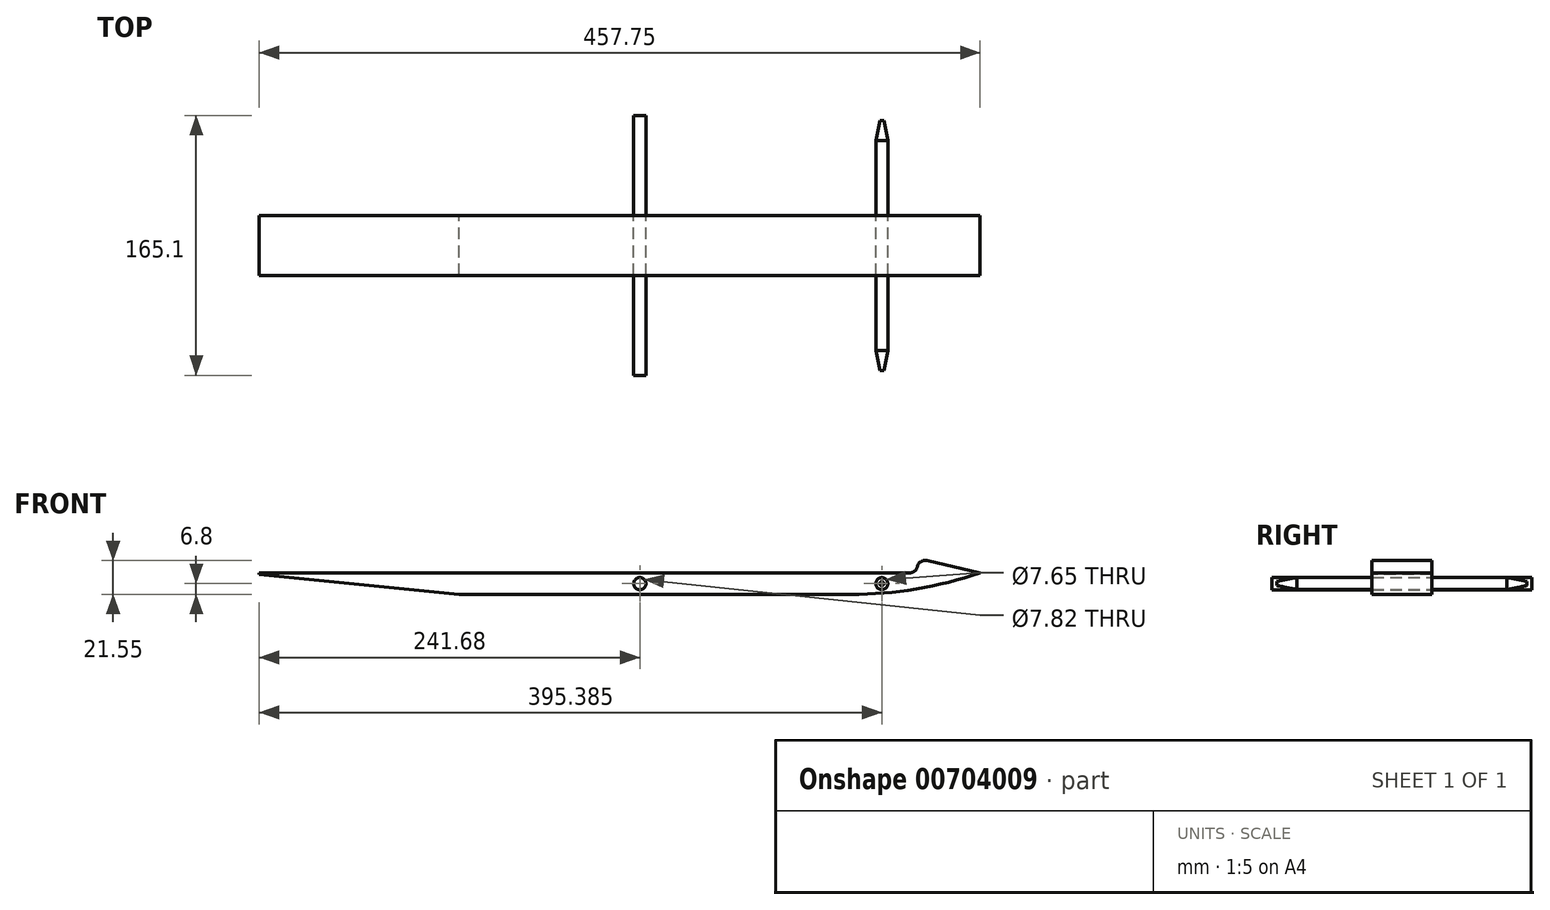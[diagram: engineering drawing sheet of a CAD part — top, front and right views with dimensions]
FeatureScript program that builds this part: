
annotation { "Feature Type Name" : "Feature", "Feature Type Description" : "" }
export const myFeature = defineFeature(function(context is Context, id is Id, definition is map)
    precondition{}
    {
        {
            var Q0;
            Q0=qCreatedBy(makeId("Front.planeOp"),FACE);
            var sketch = newSketch(context, id + "F0", { "sketchPlane" : qUnion([Q0])});
            skLineSegment(sketch, "E0.bottom", {"start": v(-241.68, -6.8) * mm, "end": v(216.07, -6.8) * mm});
            skLineSegment(sketch, "E0.top", {"start": v(-241.68, 6.8) * mm, "end": v(216.07, 6.8) * mm});
            skLineSegment(sketch, "E0.left", {"start": v(-241.68, -6.8) * mm, "end": v(-241.68, 6.8) * mm});
            skLineSegment(sketch, "E0.right", {"start": v(216.07, -6.8) * mm, "end": v(216.07, 6.8) * mm});
            skCircle(sketch, "E1", {"center": v(153.7, 0) * mm, "radius": 3.83 * mm});
            skCircle(sketch, "E2", {"center": v(0, 0) * mm, "radius": 3.9 * mm});
            skLineSegment(sketch, "E3", {"start": v(216.07, 6.8) * mm, "end": v(177.42, 15.76) * mm});
            skLineSegment(sketch, "E4", {"start": v(177.42, 15.76) * mm, "end": v(175.35, 6.8) * mm});
            skSolve(sketch);
        }
        {
            var Q0;
            Q0=makeQuery(id+"F0.imprint","IMPRINT",FACE,{"disambiguationData":[TD([[makeQuery(id+"F0.imprint","IMPRINT",EDGE,{"derivedFrom":sQuery(id+"F0.wireOp",EDGE,"E2")}),1.0]])]});
            extrude(context, id + "F1", {"entities" : qUnion([Q0]), "endBound" : BoundingType.SYMMETRIC, "depth" : 165.1 * mm, "offsetDistance" : 25.4 * mm});
        }
        {
            var Q0;
            Q0=makeQuery(id+"F0.imprint","IMPRINT",FACE,{"disambiguationData":[TD([[makeQuery(id+"F0.imprint","IMPRINT",EDGE,{"derivedFrom":sQuery(id+"F0.wireOp",EDGE,"E1")}),1.0]])]});
            extrude(context, id + "F2", {"entities" : qUnion([Q0]), "endBound" : BoundingType.SYMMETRIC, "depth" : 158.75 * mm, "offsetDistance" : 25.4 * mm});
        }
        {
            var Q0;
            Q0=makeQuery(id+"F0.imprint","IMPRINT",FACE,{"disambiguationData":[TD([[makeQuery(id+"F0.imprint","IMPRINT",EDGE,{"derivedFrom":sQuery(id+"F0.wireOp",EDGE,"E0.bottom")}),1.0]])]});
            var Q1;
            {var subQ0=sQuery(id+"F0.wireOp",EDGE,"E3");Q1=makeQuery(id+"F0.imprint","IMPRINT",FACE,{"disambiguationData":[TD([[makeQuery(id+"F0.imprint","IMPRINT",EDGE,{"derivedFrom":subQ0}),1.0]])]});}
            extrude(context, id + "F3", {"entities" : qUnion([Q0, Q1]), "endBound" : BoundingType.SYMMETRIC, "depth" : 38.1 * mm, "offsetDistance" : 25.4 * mm});
        }
        {
            var Q0;
            Q0=makeQuery(id+"F3.opExtrude","SWEPT_EDGE",EDGE,{"disambiguationData":[OSD([sQuery(id+"F0.wireOp",EDGE,"E0.bottom"),sQuery(id+"F0.wireOp",EDGE,"E0.right")])]});
            fillet(context, id + "F4", {"entities" : qUnion([Q0]), "radius" : 254 * mm, "tangentPropagation" : true, "allowEdgeOverflow" : false});
        }
        {
            var Q0;
            Q0=makeQuery(id+"F3.opExtrude","SWEPT_EDGE",EDGE,{"disambiguationData":[OSD([sQuery(id+"F0.wireOp",EDGE,"E0.top"),sQuery(id+"F0.wireOp",EDGE,"E4")])]});
            var Q1;
            Q1=makeQuery(id+"F3.opExtrude","SWEPT_EDGE",EDGE,{"disambiguationData":[OSD([sQuery(id+"F0.wireOp",EDGE,"E3"),sQuery(id+"F0.wireOp",EDGE,"E4")])]});
            fillet(context, id + "F5", {"entities" : qUnion([Q0, Q1]), "radius" : 5.08 * mm, "tangentPropagation" : true, "allowEdgeOverflow" : false});
        }
        {
            var Q0;
            Q0=makeQuery(id+"F3.opExtrude","SWEPT_EDGE",EDGE,{"disambiguationData":[OSD([sQuery(id+"F0.wireOp",EDGE,"E0.bottom"),sQuery(id+"F0.wireOp",EDGE,"E0.left")])]});
            chamfer(context, id + "F6", {"entities" : qUnion([Q0]), "chamferType" : ChamferType.TWO_OFFSETS, "width1" : 127 * mm, "oppositeDirection" : false, "width2" : 12.7 * mm, "tangentPropagation" : true});
        }
        {
            var Q0;
            Q0=makeQuery(id+"F2.opExtrude","CAP_FACE",FACE,{"disambiguationData":[OSD([sQuery(id+"F0.wireOp",EDGE,"E1")])],"isStart":true});
            var Q1;
            Q1=makeQuery(id+"F2.opExtrude","CAP_EDGE",EDGE,{"disambiguationData":[OSD([sQuery(id+"F0.wireOp",EDGE,"E1")])],"isStart":false});
            chamfer(context, id + "F7", {"entities" : qUnion([Q0, Q1]), "chamferType" : ChamferType.TWO_OFFSETS, "width1" : 12.7 * mm, "oppositeDirection" : false, "width2" : 2.54 * mm, "tangentPropagation" : true});
        }
    });
